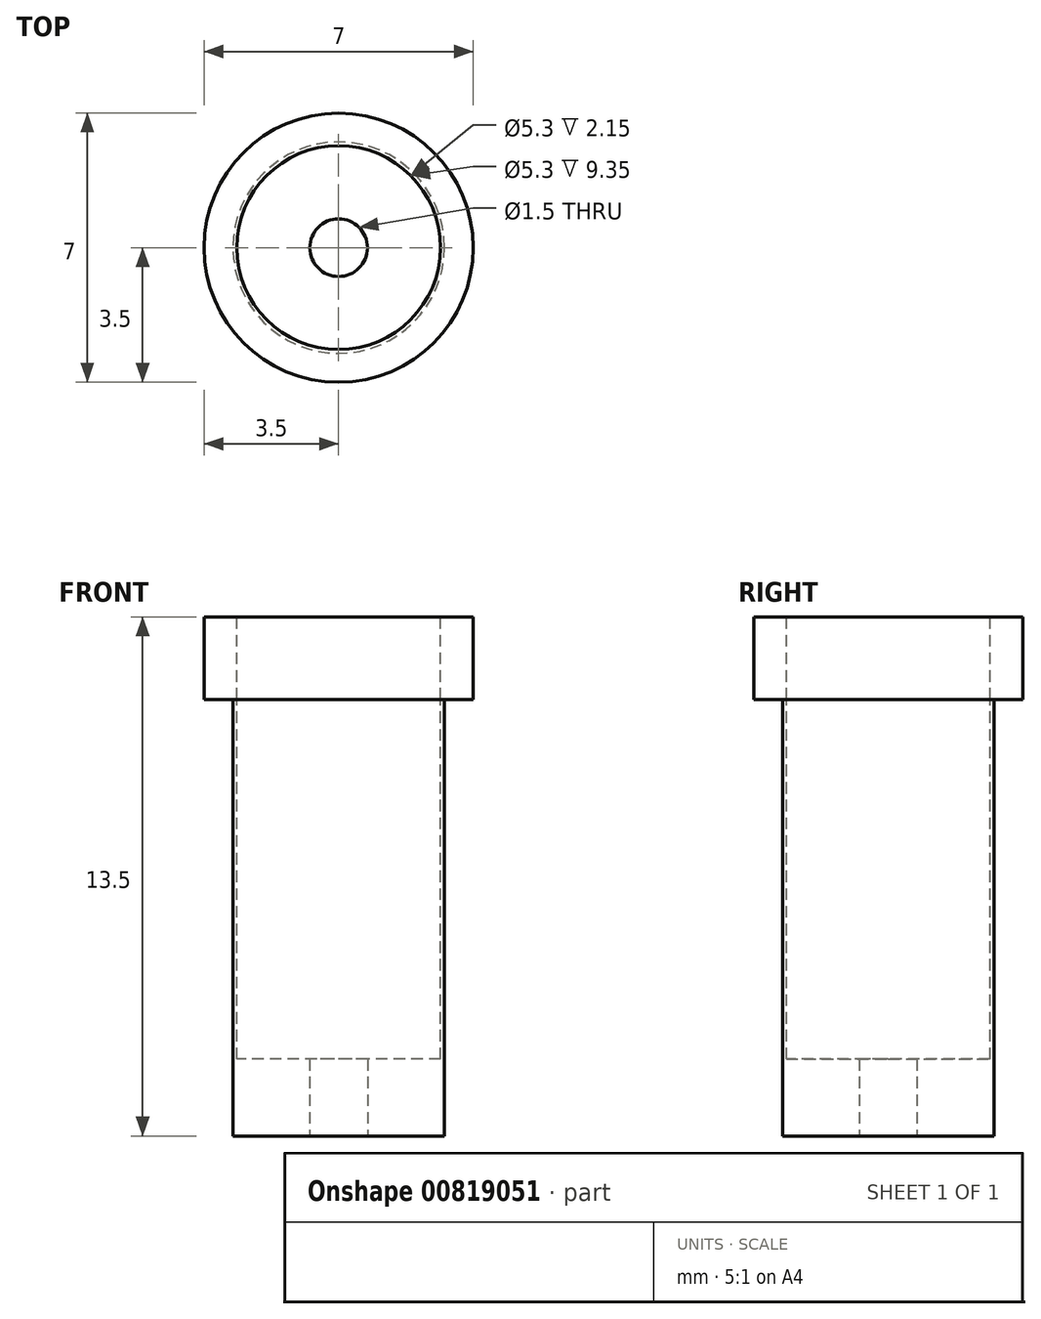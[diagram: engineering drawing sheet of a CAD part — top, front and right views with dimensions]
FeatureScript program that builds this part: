
annotation { "Feature Type Name" : "Feature", "Feature Type Description" : "" }
export const myFeature = defineFeature(function(context is Context, id is Id, definition is map)
    precondition{}
    {
        {
            var Q0;
            Q0=qCreatedBy(makeId("Top.planeOp"),FACE);
            var sketch = newSketch(context, id + "F0", { "sketchPlane" : qUnion([Q0])});
            skCircle(sketch, "E0", {"center": v(0, 0) * mm, "radius": 2.75 * mm});
            skSolve(sketch);
        }
        {
            var Q0;
            Q0 = qSketchRegion(id + "F0", true);
            extrude(context, id + "F1", {"entities" : qUnion([Q0]), "oppositeDirection" : true, "depth" : 11.35 * mm, "offsetDistance" : 25 * mm});
        }
        {
            var Q0;
            Q0=qCreatedBy(makeId("Top.planeOp"),FACE);
            var sketch = newSketch(context, id + "F2", { "sketchPlane" : qUnion([Q0])});
            skCircle(sketch, "E1", {"center": v(0, 0) * mm, "radius": 3.5 * mm});
            skSolve(sketch);
        }
        {
            var Q0;
            Q0=makeQuery(id+"F2.imprint","IMPRINT",FACE,{"disambiguationData":[TD([[makeQuery(id+"F2.imprint","IMPRINT",EDGE,{"derivedFrom":sQuery(id+"F2.wireOp",EDGE,"E1")}),1.0]])]});
            var Q1;
            Q1=sQuery(id+"F2.wireOp",EDGE,"E1");
            extrude(context, id + "F3", {"entities" : qUnion([Q0]), "surfaceEntities" : qUnion([Q1]), "depth" : 2.15 * mm, "offsetDistance" : 25 * mm});
        }
        {
            var Q0;
            Q0=makeQuery(id+"F3.opExtrude","CAP_FACE",FACE,{"disambiguationData":[OSD([sQuery(id+"F2.wireOp",EDGE,"E1")])],"isStart":false});
            var sketch = newSketch(context, id + "F4", { "sketchPlane" : qUnion([Q0])});
            skCircle(sketch, "E2", {"center": v(0, 0) * mm, "radius": 2.65 * mm});
            skSolve(sketch);
        }
        {
            var Q0;
            Q0=makeQuery(id+"F4.imprint","IMPRINT",FACE,{"disambiguationData":[TD([[makeQuery(id+"F4.imprint","IMPRINT",EDGE,{"derivedFrom":sQuery(id+"F4.wireOp",EDGE,"E2")}),1.0]])]});
            extrude(context, id + "F5", {"entities" : qUnion([Q0]), "operationType" : NewBodyOperationType.REMOVE, "oppositeDirection" : true, "depth" : 11.5 * mm, "offsetDistance" : 25 * mm});
        }
        {
            var Q0;
            Q0=makeQuery(id+"F1.opExtrude","CAP_FACE",FACE,{"disambiguationData":[OSD([sQuery(id+"F0.wireOp",EDGE,"E0")])],"isStart":false});
            var sketch = newSketch(context, id + "F6", { "sketchPlane" : qUnion([Q0])});
            skCircle(sketch, "E3", {"center": v(0, 0) * mm, "radius": 0.75 * mm});
            skSolve(sketch);
        }
        {
            var Q0;
            Q0 = qSketchRegion(id + "F6", true);
            extrude(context, id + "F7", {"entities" : qUnion([Q0]), "operationType" : NewBodyOperationType.REMOVE, "endBound" : BoundingType.THROUGH_ALL, "oppositeDirection" : true, "depth" : 25 * mm, "offsetDistance" : 25 * mm});
        }
    });
